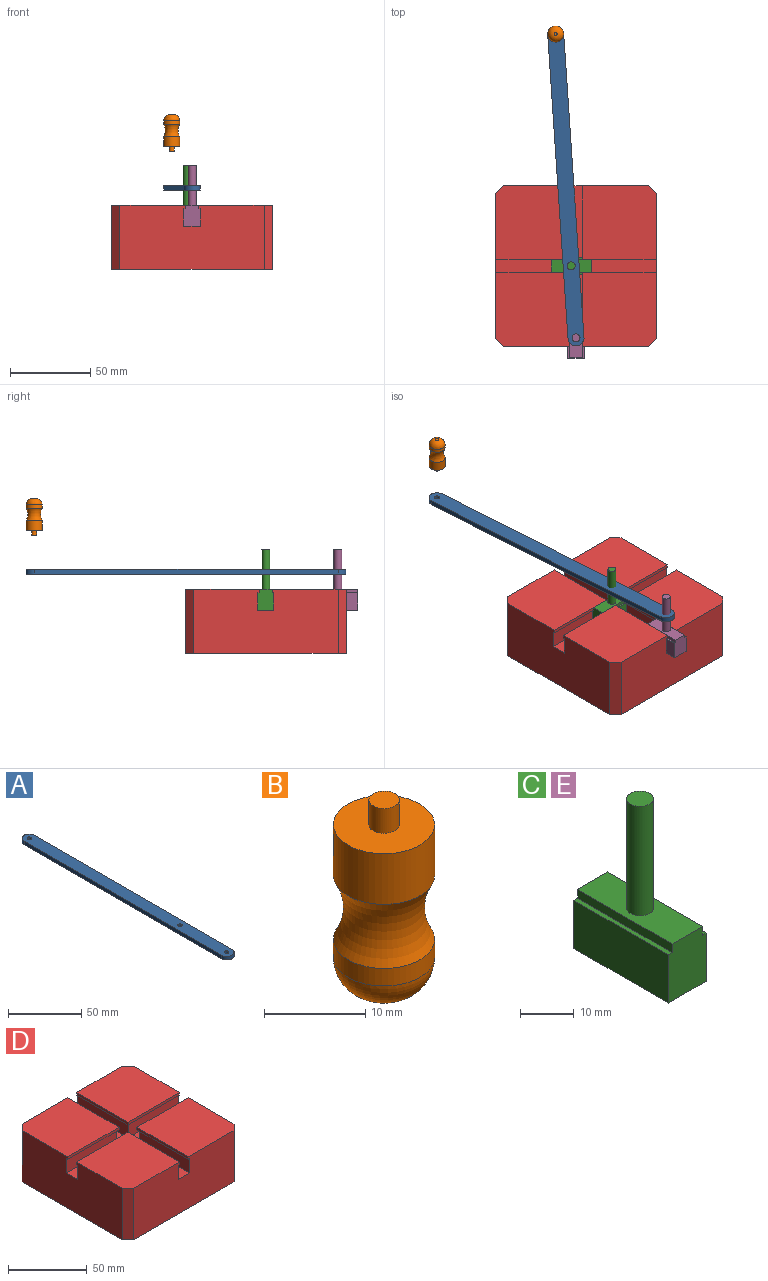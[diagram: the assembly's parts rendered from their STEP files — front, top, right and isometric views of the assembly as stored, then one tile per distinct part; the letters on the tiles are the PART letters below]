
ASSEMBLY  parts=5 mates=5
PART A: 9 faces, bbox 10x200x3 mm
  f0: cylinder r=5mm len=10mm, axis (0,0,-1), area 47.1mm2, adj f1,f6,f7,f8
  f1: plane 190x3mm, normal (-1,0,0), area 570mm2, adj f0,f2,f7,f8
  f2: cylinder r=5mm len=10mm, axis (0,0,-1), area 47.1mm2, adj f1,f6,f7,f8
  f3: cylinder r=1.5mm len=3mm, axis (0,0,-1), area 28.3mm2, adj f7,f8
  f4: cylinder r=1.5mm len=3mm, axis (0,0,-1), area 28.3mm2, adj f7,f8
  f5: cylinder r=1.5mm len=3mm, axis (0,0,-1), area 28.3mm2, adj f7,f8
  f6: plane 190x3mm, normal (1,0,0), area 570mm2, adj f0,f2,f7,f8
  f7: plane 200x10mm, normal (0,0,1), area 1957.3mm2, adj f0,f1,f2,f3,f4,f5,f6
  f8: plane 200x10mm, normal (0,0,-1), area 1957.3mm2, adj f0,f1,f2,f3,f4,f5,f6
PART B: 8 faces, bbox 13.7x13.7x23 mm
  f0: plane 2x2mm, normal (0,0,-1), area 3.1mm2, adj f1
  f1: torus R=1mm, axis (0,0,-1), area 140mm2, adj f0,f2
  f2: cylinder r=5mm len=10mm, axis (0,0,-1), area 66.8mm2, adj f1,f3
  f3: torus R=12mm, axis (0,0,-1), area 220.3mm2, adj f2,f4
  f4: cylinder r=5mm len=10mm, axis (0,0,-1), area 192.5mm2, adj f3,f5
  f5: plane 10x10mm, normal (0,0,1), area 71.5mm2, adj f4,f6
  f6: cylinder r=1.5mm len=3mm, axis (0,0,-1), area 28.3mm2, adj f5,f7
  f7: plane 3x3mm, normal (0,0,1), area 7.1mm2, adj f6
PART C: 12 faces, bbox 10x25x38 mm
  f0: plane 25x2mm, normal (-1,0,0), area 50mm2, adj f1,f7,f8,f9
  f1: plane 25x1mm, normal (0,0,1), area 25mm2, adj f0,f2,f8,f9
  f2: plane 25x11mm, normal (-1,0,0), area 275mm2, adj f1,f3,f8,f9
  f3: plane 25x10mm, normal (0,0,-1), area 250mm2, adj f2,f4,f8,f9
  f4: plane 25x11mm, normal (1,0,0), area 275mm2, adj f3,f5,f8,f9
  f5: plane 25x1mm, normal (0,0,1), area 25mm2, adj f4,f6,f8,f9
  f6: plane 25x2mm, normal (1,0,0), area 50mm2, adj f5,f7,f8,f9
  f7: plane 25x8mm, normal (0,0,1), area 180.4mm2, adj f0,f6,f8,f9,f10
  f8: plane 13x10mm, normal (0,-1,0), area 126mm2, adj f0,f1,f2,f3,f4,f5,f6,f7
  f9: plane 13x10mm, normal (0,1,0), area 126mm2, adj f0,f1,f2,f3,f4,f5,f6,f7
  f10: cylinder r=2.5mm len=25mm, axis (0,0,-1), area 392.7mm2, adj f7,f11
  f11: plane 5x5mm, normal (0,0,1), area 19.6mm2, adj f10
PART D: 34 faces, bbox 100x100x40 mm
  f0: plane 46x46mm, normal (0,0,1), area 2103.5mm2, adj f4,f6,f11,f17,f27
  f1: plane 46x46mm, normal (0,0,1), area 2103.5mm2, adj f5,f7,f11,f15,f30
  f2: plane 46x46mm, normal (0,0,-1), area 91mm2, adj f5,f7,f8,f11,f30,f33
  f3: plane 46x46mm, normal (0,0,-1), area 91mm2, adj f4,f6,f9,f11,f27,f28
  f4: plane 90x40mm, normal (1,0,0), area 3474mm2, adj f0,f3,f10,f14,f17,f18,f23,f25
  f5: plane 90x40mm, normal (-1,0,0), area 3474mm2, adj f1,f2,f13,f14,f15,f16,f21,f23
  f6: plane 46x2mm, normal (-1,0,0), area 92mm2, adj f0,f3,f11,f27
  f7: plane 46x2mm, normal (1,0,0), area 92mm2, adj f1,f2,f11,f30
  f8: plane 45x11mm, normal (1,0,0), area 495mm2, adj f2,f11,f23,f33
  f9: plane 45x11mm, normal (-1,0,0), area 495mm2, adj f3,f11,f23,f28
  f10: plane 46x46mm, normal (0,0,1), area 2103.5mm2, adj f4,f12,f18,f19,f29
  f11: plane 90x40mm, normal (0,1,0), area 3474mm2, adj f0,f1,f2,f3,f6,f7,f8,f9
  f12: plane 90x40mm, normal (0,-1,0), area 3474mm2, adj f10,f13,f14,f16,f18,f19,f20,f21
  f13: plane 46x46mm, normal (0,0,1), area 2103.5mm2, adj f5,f12,f16,f20,f31
  f14: plane 100x100mm, normal (0,0,-1), area 9950mm2, adj f4,f5,f11,f12,f15,f16,f17,f18
  f15: plane 40x5mm, normal (-0.71,0.71,0), area 282.8mm2, adj f1,f5,f11,f14
  f16: plane 40x5mm, normal (-0.71,-0.71,0), area 282.8mm2, adj f5,f12,f13,f14
  f17: plane 40x5mm, normal (0.71,0.71,0), area 282.8mm2, adj f0,f4,f11,f14
  f18: plane 40x5mm, normal (0.71,-0.71,0), area 282.8mm2, adj f4,f10,f12,f14
  f19: plane 46x2mm, normal (-1,0,0), area 92mm2, adj f10,f12,f25,f29
  f20: plane 46x2mm, normal (1,0,0), area 92mm2, adj f12,f13,f21,f31
  f21: plane 46x46mm, normal (0,0,-1), area 91mm2, adj f5,f12,f20,f22,f31,f32
  f22: plane 45x11mm, normal (1,0,0), area 495mm2, adj f12,f21,f23,f32
  f23: plane 100x100mm, normal (0,0,1), area 1900mm2, adj f4,f5,f8,f9,f11,f12,f22,f24
  f24: plane 45x11mm, normal (-1,0,0), area 495mm2, adj f12,f23,f25,f26
  f25: plane 46x46mm, normal (0,0,-1), area 91mm2, adj f4,f12,f19,f24,f26,f29
  f26: plane 45x11mm, normal (0,1,0), area 495mm2, adj f4,f23,f24,f25
  f27: plane 46x2mm, normal (0,-1,0), area 92mm2, adj f0,f3,f4,f6
  f28: plane 45x11mm, normal (0,-1,0), area 495mm2, adj f3,f4,f9,f23
  f29: plane 46x2mm, normal (0,1,0), area 92mm2, adj f4,f10,f19,f25
  f30: plane 46x2mm, normal (0,-1,0), area 92mm2, adj f1,f2,f5,f7
  f31: plane 46x2mm, normal (0,1,0), area 92mm2, adj f5,f13,f20,f21
  f32: plane 45x11mm, normal (0,1,0), area 495mm2, adj f5,f21,f22,f23
  f33: plane 45x11mm, normal (0,-1,0), area 495mm2, adj f2,f5,f8,f23
PART E: same geometry as C
PLACE A rot(axis=(0,0,1),3.8deg) t=(-86.9,-46.5,50.76)mm
PLACE B rot(axis=(1,0.03,0),180deg) t=(-36.52,212.02,137.12)mm
PLACE C rot(axis=(0,0,-1),90deg) t=(-10.02,2.9,33.76)mm
PLACE D t=(-19.52,2.9,1.26)mm fixed
PLACE E t=(-19.52,-29.5,33.76)mm
MATE slider B.f1 <-> A.f0  axis (0,0,-1) through (-32.2,147.58,74.97)mm
MATE revolute E.f10 <-> A.f2  axis (0,0,-1) through (-19.52,-42,53.76)mm
MATE slider D.f5 <-> C.f8  axis (-1,0,0) through (-69.52,2.9,28.26)mm
MATE slider E.f8 <-> D.f12  axis (0,-1,0) through (-19.52,-54.5,28.26)mm
MATE revolute A.f5 <-> C.f10  axis (0,0,1) through (-22.52,2.9,53.76)mm
